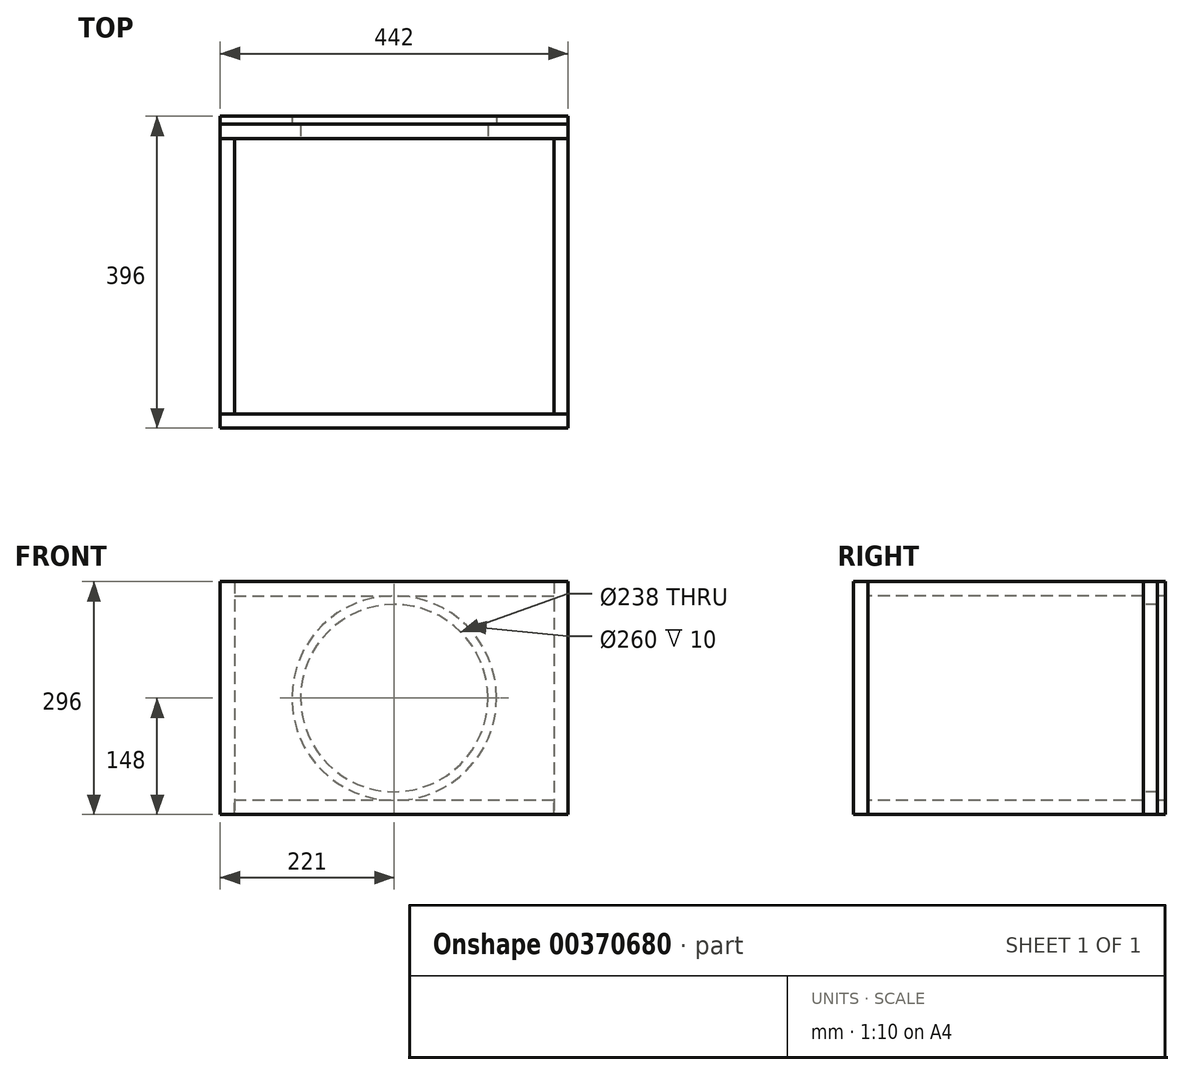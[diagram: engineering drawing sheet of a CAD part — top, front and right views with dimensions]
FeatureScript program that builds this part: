
annotation { "Feature Type Name" : "Feature", "Feature Type Description" : "" }
export const myFeature = defineFeature(function(context is Context, id is Id, definition is map)
    precondition{}
    {
        {
            var Q0;
            Q0=qCreatedBy(makeId("Front.planeOp"),FACE);
            var sketch = newSketch(context, id + "F0", { "sketchPlane" : qUnion([Q0])});
            skLineSegment(sketch, "E0.bottom", {"start": v(221, -148) * mm, "end": v(-221, -148) * mm});
            skLineSegment(sketch, "E0.top", {"start": v(221, 148) * mm, "end": v(-221, 148) * mm});
            skLineSegment(sketch, "E0.left", {"start": v(221, -148) * mm, "end": v(221, 148) * mm});
            skLineSegment(sketch, "E0.right", {"start": v(-221, -148) * mm, "end": v(-221, 148) * mm});
            skPoint(sketch, "E0.middle", {"position": v(0, 0) * mm});
            skSolve(sketch);
        }
        {
            var Q0;
            Q0 = qSketchRegion(id + "F0", true);
            extrude(context, id + "F1", {"entities" : qUnion([Q0]), "depth" : 18 * mm});
        }
        {
            var Q0;
            Q0=makeQuery(id+"F1.opExtrude","CAP_FACE",FACE,{"disambiguationData":[OSD([sQuery(id+"F0.wireOp",EDGE,"E0.bottom"),sQuery(id+"F0.wireOp",EDGE,"E0.top"),sQuery(id+"F0.wireOp",EDGE,"E0.left"),sQuery(id+"F0.wireOp",EDGE,"E0.right")])],"isStart":true});
            var sketch = newSketch(context, id + "F2", { "sketchPlane" : qUnion([Q0])});
            skLineSegment(sketch, "E1.bottom", {"start": v(-221, 148) * mm, "end": v(-203, 148) * mm});
            skLineSegment(sketch, "E1.top", {"start": v(-221, -148) * mm, "end": v(-203, -148) * mm});
            skLineSegment(sketch, "E1.left", {"start": v(-221, 148) * mm, "end": v(-221, -148) * mm});
            skLineSegment(sketch, "E1.right", {"start": v(-203, 148) * mm, "end": v(-203, -148) * mm});
            skSolve(sketch);
        }
        {
            var Q0;
            Q0 = qSketchRegion(id + "F2", true);
            extrude(context, id + "F3", {"entities" : qUnion([Q0]), "depth" : 350 * mm});
        }
        {
            var Q0;
            Q0=makeQuery(id+"F1.opExtrude","CAP_FACE",FACE,{"disambiguationData":[OSD([sQuery(id+"F0.wireOp",EDGE,"E0.bottom"),sQuery(id+"F0.wireOp",EDGE,"E0.top"),sQuery(id+"F0.wireOp",EDGE,"E0.left"),sQuery(id+"F0.wireOp",EDGE,"E0.right")])],"isStart":true});
            var sketch = newSketch(context, id + "F4", { "sketchPlane" : qUnion([Q0])});
            skLineSegment(sketch, "E2.bottom", {"start": v(221, 148) * mm, "end": v(203, 148) * mm});
            skLineSegment(sketch, "E2.top", {"start": v(221, -148) * mm, "end": v(203, -148) * mm});
            skLineSegment(sketch, "E2.left", {"start": v(221, 148) * mm, "end": v(221, -148) * mm});
            skLineSegment(sketch, "E2.right", {"start": v(203, 148) * mm, "end": v(203, -148) * mm});
            skSolve(sketch);
        }
        {
            var Q0;
            Q0 = qSketchRegion(id + "F4", true);
            extrude(context, id + "F5", {"entities" : qUnion([Q0]), "depth" : 350 * mm});
        }
        {
            var Q0;
            Q0=makeQuery(id+"F1.opExtrude","CAP_FACE",FACE,{"disambiguationData":[OSD([sQuery(id+"F0.wireOp",EDGE,"E0.bottom"),sQuery(id+"F0.wireOp",EDGE,"E0.top"),sQuery(id+"F0.wireOp",EDGE,"E0.left"),sQuery(id+"F0.wireOp",EDGE,"E0.right")])],"isStart":true});
            var sketch = newSketch(context, id + "F6", { "sketchPlane" : qUnion([Q0])});
            skLineSegment(sketch, "E3.bottom", {"start": v(203, 148) * mm, "end": v(-203, 148) * mm});
            skLineSegment(sketch, "E3.top", {"start": v(203, 130) * mm, "end": v(-203, 130) * mm});
            skLineSegment(sketch, "E3.left", {"start": v(203, 148) * mm, "end": v(203, 130) * mm});
            skLineSegment(sketch, "E3.right", {"start": v(-203, 148) * mm, "end": v(-203, 130) * mm});
            skSolve(sketch);
        }
        {
            var Q0;
            Q0=makeQuery(id+"F6.imprint","IMPRINT",FACE,{"disambiguationData":[TD([[makeQuery(id+"F6.imprint","IMPRINT",EDGE,{"derivedFrom":sQuery(id+"F6.wireOp",EDGE,"E3.top")}),1.0]])]});
            var sketch = newSketch(context, id + "F7", { "sketchPlane" : qUnion([Q0])});
            skLineSegment(sketch, "E4.bottom", {"start": v(-203, -148) * mm, "end": v(203, -148) * mm});
            skLineSegment(sketch, "E4.top", {"start": v(-203, -130) * mm, "end": v(203, -130) * mm});
            skLineSegment(sketch, "E4.left", {"start": v(-203, -148) * mm, "end": v(-203, -130) * mm});
            skLineSegment(sketch, "E4.right", {"start": v(203, -148) * mm, "end": v(203, -130) * mm});
            skSolve(sketch);
        }
        {
            var Q0;
            Q0 = qSketchRegion(id + "F6", true);
            extrude(context, id + "F8", {"entities" : qUnion([Q0]), "depth" : 350 * mm});
        }
        {
            var Q0;
            Q0 = qSketchRegion(id + "F7", true);
            extrude(context, id + "F9", {"entities" : qUnion([Q0]), "depth" : 350 * mm});
        }
        {
            var Q0;
            Q0=makeQuery(id+"F8.opExtrude","CAP_FACE",FACE,{"disambiguationData":[OSD([sQuery(id+"F6.wireOp",EDGE,"E3.bottom"),sQuery(id+"F6.wireOp",EDGE,"E3.top"),sQuery(id+"F6.wireOp",EDGE,"E3.left"),sQuery(id+"F6.wireOp",EDGE,"E3.right")])],"isStart":false});
            var sketch = newSketch(context, id + "F10", { "sketchPlane" : qUnion([Q0])});
            skLineSegment(sketch, "E5.bottom", {"start": v(-221, 148) * mm, "end": v(221, 148) * mm});
            skLineSegment(sketch, "E5.top", {"start": v(-221, -148) * mm, "end": v(221, -148) * mm});
            skLineSegment(sketch, "E5.left", {"start": v(-221, 148) * mm, "end": v(-221, -148) * mm});
            skLineSegment(sketch, "E5.right", {"start": v(221, 148) * mm, "end": v(221, -148) * mm});
            skCircle(sketch, "E6", {"center": v(0, 0) * mm, "radius": 119 * mm});
            skSolve(sketch);
        }
        {
            var Q0;
            Q0 = qSketchRegion(id + "F10", true);
            extrude(context, id + "F11", {"entities" : qUnion([Q0]), "depth" : 18 * mm});
        }
        {
            var Q0;
            Q0=makeQuery(id+"F11.opExtrude","SWEPT_BODY",BODY,{"disambiguationData":[OSD([sQuery(id+"F10.wireOp",EDGE,"E5.bottom"),sQuery(id+"F10.wireOp",EDGE,"E5.top"),sQuery(id+"F10.wireOp",EDGE,"E5.left"),sQuery(id+"F10.wireOp",EDGE,"E5.right"),sQuery(id+"F10.wireOp",EDGE,"E6")])]});
            transform(context, id + "F12", {"entities" : qUnion([Q0]), "transformType" : TransformType.TRANSLATION_3D, "dx" : 0 * mm, "dy" : 18 * mm, "dz" : 0 * mm, "makeCopy" : true});
        }
        {
            var Q0;
            Q0=makeQuery(id+"F12.opPattern","COPY",BODY,{"derivedFrom":makeQuery(id+"F11.opExtrude","SWEPT_BODY",BODY,{"disambiguationData":[OSD([sQuery(id+"F10.wireOp",EDGE,"E5.bottom"),sQuery(id+"F10.wireOp",EDGE,"E5.top"),sQuery(id+"F10.wireOp",EDGE,"E5.left"),sQuery(id+"F10.wireOp",EDGE,"E5.right"),sQuery(id+"F10.wireOp",EDGE,"E6")])]}),"instanceName":"1"});
            deleteBodies(context, id + "F13", {"entities" : qUnion([Q0])});
        }
        {
            var Q0;
            Q0=makeQuery(id+"F11.opExtrude","CAP_FACE",FACE,{"disambiguationData":[OSD([sQuery(id+"F10.wireOp",EDGE,"E5.bottom"),sQuery(id+"F10.wireOp",EDGE,"E5.top"),sQuery(id+"F10.wireOp",EDGE,"E5.left"),sQuery(id+"F10.wireOp",EDGE,"E5.right"),sQuery(id+"F10.wireOp",EDGE,"E6")])],"isStart":false});
            var sketch = newSketch(context, id + "F14", { "sketchPlane" : qUnion([Q0])});
            skLineSegment(sketch, "E7.bottom", {"start": v(-221, 148) * mm, "end": v(221, 148) * mm});
            skLineSegment(sketch, "E7.top", {"start": v(-221, -148) * mm, "end": v(221, -148) * mm});
            skLineSegment(sketch, "E7.left", {"start": v(-221, 148) * mm, "end": v(-221, -148) * mm});
            skLineSegment(sketch, "E7.right", {"start": v(221, 148) * mm, "end": v(221, -148) * mm});
            skCircle(sketch, "E8", {"center": v(0, 0) * mm, "radius": 130 * mm});
            skSolve(sketch);
        }
        {
            var Q0;
            Q0 = qSketchRegion(id + "F14", true);
            extrude(context, id + "F15", {"entities" : qUnion([Q0]), "depth" : 10 * mm});
        }
    });
